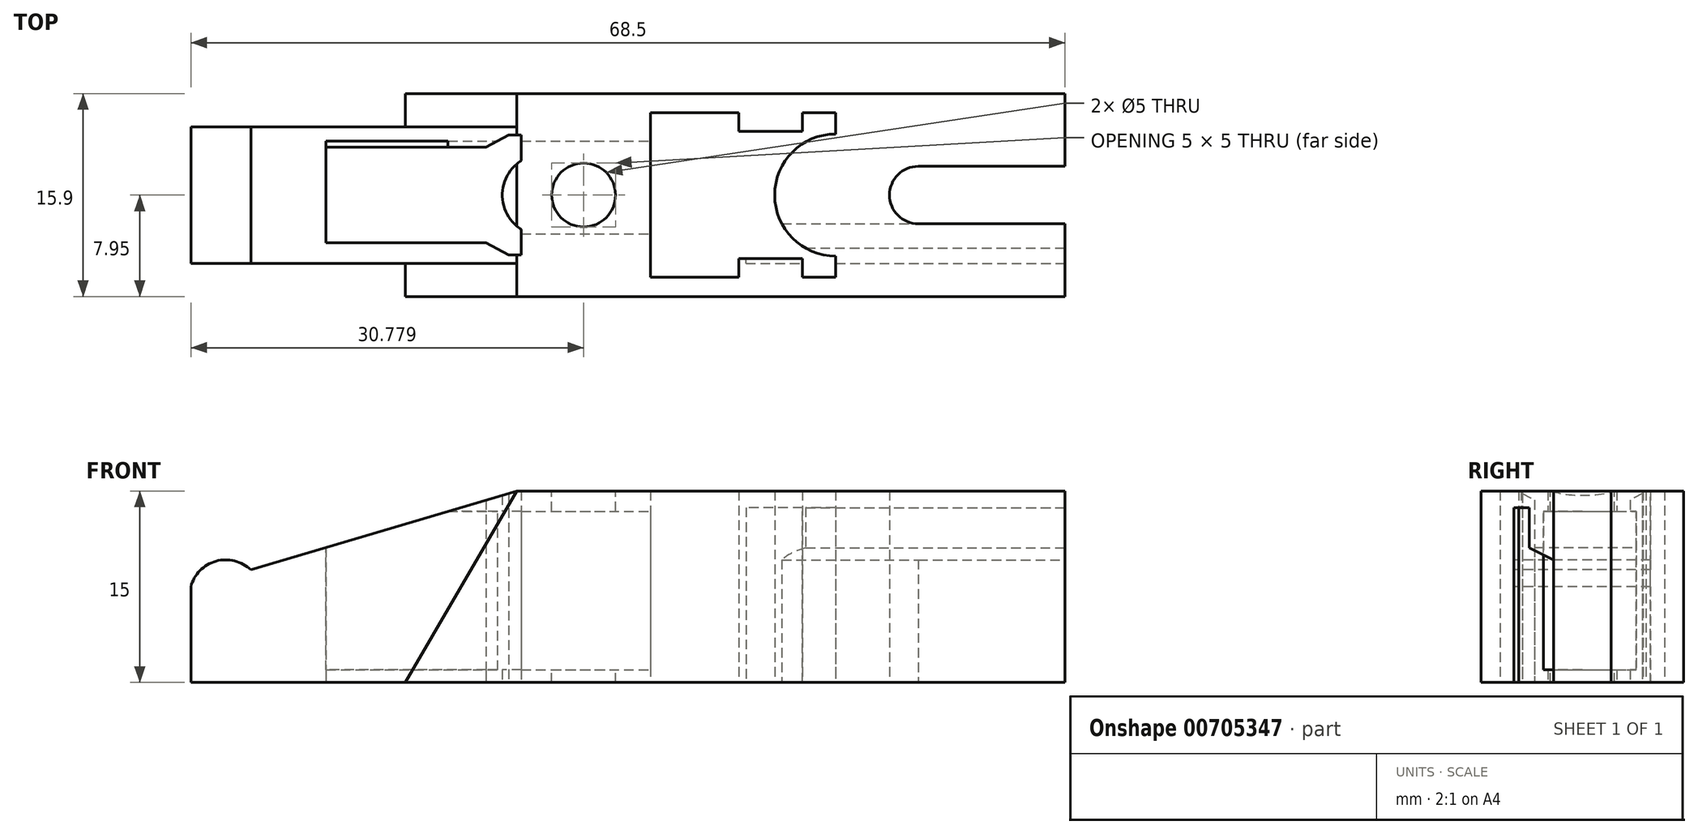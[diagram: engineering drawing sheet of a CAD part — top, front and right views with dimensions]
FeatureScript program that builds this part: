
annotation { "Feature Type Name" : "Feature", "Feature Type Description" : "" }
export const myFeature = defineFeature(function(context is Context, id is Id, definition is map)
    precondition{}
    {
        {
            var Q0;
            Q0=qCreatedBy(makeId("Top.planeOp"),FACE);
            var sketch = newSketch(context, id + "F0", { "sketchPlane" : qUnion([Q0])});
            skLineSegment(sketch, "E0", {"start": v(0, 0) * mm, "end": v(0, 10.7) * mm});
            skLineSegment(sketch, "E1", {"start": v(0, 10.7) * mm, "end": v(16.8, 10.7) * mm});
            skLineSegment(sketch, "E2", {"start": v(68.5, 13.3) * mm, "end": v(68.5, 7.6) * mm});
            skLineSegment(sketch, "E3", {"start": v(68.5, 7.6) * mm, "end": v(57, 7.6) * mm});
            skLineSegment(sketch, "E4", {"start": v(57, 3.1) * mm, "end": v(68.5, 3.1) * mm});
            skLineSegment(sketch, "E5", {"start": v(0, 0) * mm, "end": v(16.8, 0) * mm});
            skLineSegment(sketch, "E6", {"start": v(16.8, 0) * mm, "end": v(16.8, -2.6) * mm});
            skLineSegment(sketch, "E7", {"start": v(16.8, -2.6) * mm, "end": v(68.5, -2.6) * mm});
            skLineSegment(sketch, "E8", {"start": v(68.5, -2.6) * mm, "end": v(68.5, 3.1) * mm});
            skLineSegment(sketch, "E9", {"start": v(50.53, -1.1) * mm, "end": v(50.53, 0.57) * mm});
            skLineSegment(sketch, "E10", {"start": v(25.9, 0.66) * mm, "end": v(25.9, 2.66) * mm});
            skLineSegment(sketch, "E11.MirrorCS", {"start": v(10.6, 9.1) * mm, "end": v(23.13, 9.1) * mm});
            skLineSegment(sketch, "E12.MirrorCS", {"start": v(25.9, 10.04) * mm, "end": v(25.9, 8.04) * mm});
            skArc(sketch, "E13", {"start": v(25.9, 8.04) * mm, "mid": v(24.4, 5.35) * mm, "end": v(25.9, 2.66) * mm});
            skLineSegment(sketch, "E14.MirrorCS", {"start": v(16.8, 10.7) * mm, "end": v(16.8, 13.3) * mm});
            skLineSegment(sketch, "E15.MirrorCS", {"start": v(16.8, 13.3) * mm, "end": v(68.5, 13.3) * mm});
            skLineSegment(sketch, "E16", {"start": v(36.03, -1.1) * mm, "end": v(42.93, -1.1) * mm});
            skLineSegment(sketch, "E17", {"start": v(42.93, -1.1) * mm, "end": v(42.93, 0.37) * mm});
            skLineSegment(sketch, "E18", {"start": v(42.93, 0.37) * mm, "end": v(47.93, 0.37) * mm});
            skLineSegment(sketch, "E19", {"start": v(47.93, 0.37) * mm, "end": v(47.93, -1.1) * mm});
            skLineSegment(sketch, "E20", {"start": v(47.93, -1.1) * mm, "end": v(50.53, -1.1) * mm});
            skLineSegment(sketch, "E21.MirrorCS", {"start": v(23.13, 9.1) * mm, "end": v(24.9, 10.04) * mm});
            skLineSegment(sketch, "E22.MirrorCS", {"start": v(24.9, 10.04) * mm, "end": v(25.9, 10.04) * mm});
            skPoint(sketch, "E23", {"position": v(24.4, 5.35) * mm});
            skLineSegment(sketch, "E24", {"start": v(57, 7.6) * mm, "end": v(57, 3.1) * mm, "construction": true});
            skArc(sketch, "E25", {"start": v(57, 7.6) * mm, "mid": v(54.75, 5.35) * mm, "end": v(57, 3.1) * mm});
            skLineSegment(sketch, "E26", {"start": v(0, 5.35) * mm, "end": v(68.5, 5.35) * mm, "construction": true});
            skLineSegment(sketch, "E27.MirrorCS", {"start": v(10.6, 1.6) * mm, "end": v(23.13, 1.6) * mm});
            skLineSegment(sketch, "E28.MirrorCS", {"start": v(23.13, 1.6) * mm, "end": v(24.9, 0.66) * mm});
            skLineSegment(sketch, "E29.MirrorCS", {"start": v(24.9, 0.66) * mm, "end": v(25.9, 0.66) * mm});
            skLineSegment(sketch, "E30", {"start": v(10.6, 9.1) * mm, "end": v(10.6, 1.6) * mm});
            skLineSegment(sketch, "E31", {"start": v(36.03, 11.8) * mm, "end": v(36.03, -1.1) * mm});
            skLineSegment(sketch, "E32.MirrorCS", {"start": v(36.03, 11.8) * mm, "end": v(42.93, 11.8) * mm});
            skLineSegment(sketch, "E33.MirrorCS", {"start": v(42.93, 11.8) * mm, "end": v(42.93, 10.33) * mm});
            skLineSegment(sketch, "E34.MirrorCS", {"start": v(42.93, 10.33) * mm, "end": v(47.93, 10.33) * mm});
            skLineSegment(sketch, "E35.MirrorCS", {"start": v(47.93, 10.33) * mm, "end": v(47.93, 11.8) * mm});
            skLineSegment(sketch, "E36.MirrorCS", {"start": v(47.93, 11.8) * mm, "end": v(50.53, 11.8) * mm});
            skLineSegment(sketch, "E37.MirrorCS", {"start": v(50.53, 11.8) * mm, "end": v(50.53, 10.13) * mm});
            skLineSegment(sketch, "E38", {"start": v(50.53, 10.13) * mm, "end": v(50.53, 0.57) * mm, "construction": true});
            skArc(sketch, "E39", {"start": v(50.53, 10.13) * mm, "mid": v(45.75, 5.35) * mm, "end": v(50.53, 0.57) * mm});
            skPoint(sketch, "E40", {"position": v(45.75, 5.35) * mm});
            skSolve(sketch);
        }
        {
            var Q0;
            Q0 = qSketchRegion(id + "F0", true);
            var Q1;
            Q1=makeQuery(id+"F0.imprint","IMPRINT",FACE,{"disambiguationData":[TD([[makeQuery(id+"F0.imprint","IMPRINT",EDGE,{"derivedFrom":sQuery(id+"F0.wireOp",EDGE,"E0")}),-1.0]])]});
            extrude(context, id + "F1", {"entities" : qUnion([Q0, Q1]), "depth" : 15 * mm, "offsetDistance" : 25 * mm});
        }
        {
            var Q0;
            Q0=makeQuery(id+"F1.opExtrude","SWEPT_FACE",FACE,{"disambiguationData":[OSD([sQuery(id+"F0.wireOp",EDGE,"E7")])]});
            var sketch = newSketch(context, id + "F2", { "sketchPlane" : qUnion([Q0])});
            skLineSegment(sketch, "E41", {"start": v(16.8, 0) * mm, "end": v(25.53, 15) * mm});
            skLineSegment(sketch, "E42", {"start": v(25.53, 15) * mm, "end": v(16.8, 15) * mm});
            skLineSegment(sketch, "E43", {"start": v(16.8, 15) * mm, "end": v(16.8, 0) * mm});
            skSolve(sketch);
        }
        {
            var Q0;
            Q0 = qSketchRegion(id + "F2", true);
            var Q1;
            Q1=makeQuery(id+"F1.opExtrude","SWEPT_FACE",FACE,{"disambiguationData":[OSD([sQuery(id+"F0.wireOp",EDGE,"E5")])]});
            extrude(context, id + "F3", {"entities" : qUnion([Q0]), "operationType" : NewBodyOperationType.REMOVE, "endBound" : BoundingType.UP_TO_SURFACE, "oppositeDirection" : true, "depth" : 25 * mm, "endBoundEntityFace" : qUnion([Q1]), "offsetDistance" : 25 * mm});
        }
        {
            var Q0;
            Q0=makeQuery(id+"F1.opExtrude","SWEPT_FACE",FACE,{"disambiguationData":[OSD([sQuery(id+"F0.wireOp",EDGE,"E15.MirrorCS")])]});
            var sketch = newSketch(context, id + "F4", { "sketchPlane" : qUnion([Q0])});
            skLineSegment(sketch, "E44", {"start": v(-16.8, 0) * mm, "end": v(-16.8, 15) * mm});
            skLineSegment(sketch, "E45", {"start": v(-16.8, 15) * mm, "end": v(-25.53, 15) * mm});
            skLineSegment(sketch, "E46", {"start": v(-25.53, 15) * mm, "end": v(-16.8, 0) * mm});
            skSolve(sketch);
        }
        {
            var Q0;
            Q0 = qSketchRegion(id + "F4", true);
            var Q1;
            Q1=makeQuery(id+"F1.opExtrude","SWEPT_FACE",FACE,{"disambiguationData":[OSD([sQuery(id+"F0.wireOp",EDGE,"E1")])]});
            extrude(context, id + "F5", {"entities" : qUnion([Q0]), "operationType" : NewBodyOperationType.REMOVE, "endBound" : BoundingType.UP_TO_SURFACE, "oppositeDirection" : true, "depth" : 25 * mm, "endBoundEntityFace" : qUnion([Q1]), "offsetDistance" : 25 * mm});
        }
        {
            var Q0;
            Q0=makeQuery(id+"F1.opExtrude","CAP_FACE",FACE,{"disambiguationData":[OSD([sQuery(id+"F0.wireOp",EDGE,"E0"),sQuery(id+"F0.wireOp",EDGE,"E1"),sQuery(id+"F0.wireOp",EDGE,"E2"),sQuery(id+"F0.wireOp",EDGE,"E3"),sQuery(id+"F0.wireOp",EDGE,"E4"),sQuery(id+"F0.wireOp",EDGE,"E5"),sQuery(id+"F0.wireOp",EDGE,"E6"),sQuery(id+"F0.wireOp",EDGE,"E7"),sQuery(id+"F0.wireOp",EDGE,"E8"),sQuery(id+"F0.wireOp",EDGE,"E9"),sQuery(id+"F0.wireOp",EDGE,"E10"),sQuery(id+"F0.wireOp",EDGE,"E11.MirrorCS"),sQuery(id+"F0.wireOp",EDGE,"E12.MirrorCS"),sQuery(id+"F0.wireOp",EDGE,"E13"),sQuery(id+"F0.wireOp",EDGE,"E14.MirrorCS"),sQuery(id+"F0.wireOp",EDGE,"E15.MirrorCS"),sQuery(id+"F0.wireOp",EDGE,"E16"),sQuery(id+"F0.wireOp",EDGE,"E17"),sQuery(id+"F0.wireOp",EDGE,"E18"),sQuery(id+"F0.wireOp",EDGE,"E19"),sQuery(id+"F0.wireOp",EDGE,"E20"),sQuery(id+"F0.wireOp",EDGE,"E21.MirrorCS"),sQuery(id+"F0.wireOp",EDGE,"E22.MirrorCS"),sQuery(id+"F0.wireOp",EDGE,"E25"),sQuery(id+"F0.wireOp",EDGE,"E27.MirrorCS"),sQuery(id+"F0.wireOp",EDGE,"E28.MirrorCS"),sQuery(id+"F0.wireOp",EDGE,"E29.MirrorCS"),sQuery(id+"F0.wireOp",EDGE,"E30"),sQuery(id+"F0.wireOp",EDGE,"E31"),sQuery(id+"F0.wireOp",EDGE,"E32.MirrorCS"),sQuery(id+"F0.wireOp",EDGE,"E33.MirrorCS"),sQuery(id+"F0.wireOp",EDGE,"E34.MirrorCS"),sQuery(id+"F0.wireOp",EDGE,"E35.MirrorCS"),sQuery(id+"F0.wireOp",EDGE,"E36.MirrorCS"),sQuery(id+"F0.wireOp",EDGE,"E37.MirrorCS"),sQuery(id+"F0.wireOp",EDGE,"E39")])],"isStart":false});
            var sketch = newSketch(context, id + "F6", { "sketchPlane" : qUnion([Q0])});
            skCircle(sketch, "E47", {"center": v(30.78, 5.35) * mm, "radius": 2.5 * mm});
            skPoint(sketch, "E47.centerSnap0", {"position": v(36.03, 5.35) * mm});
            skSolve(sketch);
        }
        {
            var Q0;
            Q0 = qSketchRegion(id + "F6", true);
            extrude(context, id + "F7", {"entities" : qUnion([Q0]), "operationType" : NewBodyOperationType.REMOVE, "endBound" : BoundingType.THROUGH_ALL, "oppositeDirection" : true, "depth" : 25 * mm, "offsetDistance" : 25 * mm});
        }
        {
            var Q0;
            Q0=makeQuery(id+"F1.opExtrude","SWEPT_FACE",FACE,{"disambiguationData":[OSD([sQuery(id+"F0.wireOp",EDGE,"E8")])]});
            var sketch = newSketch(context, id + "F8", { "sketchPlane" : qUnion([Q0])});
            skLineSegment(sketch, "E48", {"start": v(0, 0) * mm, "end": v(0, 13.7) * mm});
            skLineSegment(sketch, "E49", {"start": v(0, 13.7) * mm, "end": v(1.18, 13.7) * mm});
            skLineSegment(sketch, "E50", {"start": v(1.18, 13.7) * mm, "end": v(1.18, 10.55) * mm});
            skLineSegment(sketch, "E51", {"start": v(1.18, 10.55) * mm, "end": v(3.1, 9.61) * mm});
            skLineSegment(sketch, "E52", {"start": v(3.1, 9.61) * mm, "end": v(3.1, 11.46) * mm});
            skLineSegment(sketch, "E53", {"start": v(3.1, 11.46) * mm, "end": v(2.48, 11.7) * mm});
            skLineSegment(sketch, "E54", {"start": v(2.48, 11.7) * mm, "end": v(2.48, 15) * mm});
            skLineSegment(sketch, "E55", {"start": v(2.48, 15) * mm, "end": v(-2.6, 15) * mm});
            skLineSegment(sketch, "E56", {"start": v(-2.6, 15) * mm, "end": v(-2.6, 0) * mm});
            skLineSegment(sketch, "E57", {"start": v(5.37, 15.07) * mm, "end": v(5.37, -0.31) * mm, "construction": true});
            skLineSegment(sketch, "E58.MirrorCS", {"start": v(8.27, 11.7) * mm, "end": v(8.27, 15) * mm});
            skLineSegment(sketch, "E59.MirrorCS", {"start": v(7.65, 11.46) * mm, "end": v(8.27, 11.7) * mm});
            skLineSegment(sketch, "E60.MirrorCS", {"start": v(9.57, 10.55) * mm, "end": v(7.65, 9.61) * mm});
            skLineSegment(sketch, "E61.MirrorCS", {"start": v(9.57, 13.7) * mm, "end": v(9.57, 10.55) * mm});
            skLineSegment(sketch, "E62.MirrorCS", {"start": v(10.75, 13.7) * mm, "end": v(9.57, 13.7) * mm});
            skLineSegment(sketch, "E63.MirrorCS", {"start": v(10.75, 0) * mm, "end": v(10.75, 13.7) * mm});
            skLineSegment(sketch, "E64.MirrorCS", {"start": v(13.35, 15) * mm, "end": v(13.35, 0) * mm});
            skLineSegment(sketch, "E65.MirrorCS", {"start": v(8.27, 15) * mm, "end": v(13.35, 15) * mm});
            skLineSegment(sketch, "E66", {"start": v(-2.6, 0) * mm, "end": v(0, 0) * mm});
            skSolve(sketch);
        }
        {
            var Q0;
            {var subQ5=sQuery(id+"F8.wireOp",EDGE,"E48");Q0=makeQuery(id+"F8.imprint","IMPRINT",FACE,{"disambiguationData":[TD([[makeQuery(id+"F8.imprint","IMPRINT",EDGE,{"derivedFrom":subQ5}),-1.0]])]});}
            extrude(context, id + "F9", {"entities" : qUnion([Q0]), "operationType" : NewBodyOperationType.REMOVE, "oppositeDirection" : true, "depth" : 25 * mm, "offsetDistance" : 25 * mm});
        }
        {
            var Q0;
            Q0=makeQuery(id+"F1.opExtrude","SWEPT_FACE",FACE,{"disambiguationData":[OSD([sQuery(id+"F0.wireOp",EDGE,"E31")])]});
            var sketch = newSketch(context, id + "F10", { "sketchPlane" : qUnion([Q0])});
            skLineSegment(sketch, "E67.bottom", {"start": v(2.32, 13.4) * mm, "end": v(9.58, 13.4) * mm});
            skLineSegment(sketch, "E67.top", {"start": v(2.32, 0.98) * mm, "end": v(9.58, 0.98) * mm});
            skLineSegment(sketch, "E67.left", {"start": v(2.32, 13.4) * mm, "end": v(2.32, 0.98) * mm});
            skLineSegment(sketch, "E67.right", {"start": v(9.58, 13.4) * mm, "end": v(9.58, 0.98) * mm});
            skSolve(sketch);
        }
        {
            var Q0;
            Q0 = qSketchRegion(id + "F10", true);
            var Q1;
            Q1=makeQuery(id+"F1.opExtrude","SWEPT_FACE",FACE,{"disambiguationData":[OSD([sQuery(id+"F0.wireOp",EDGE,"E30")])]});
            extrude(context, id + "F11", {"entities" : qUnion([Q0]), "operationType" : NewBodyOperationType.REMOVE, "endBound" : BoundingType.UP_TO_SURFACE, "oppositeDirection" : true, "depth" : 25 * mm, "endBoundEntityFace" : qUnion([Q1]), "offsetDistance" : 25 * mm});
        }
        {
            var Q0;
            {var subQ0=sQuery(id+"F0.wireOp",EDGE,"E5");Q0=makeQuery(id+"F3.boolean.opBoolean","MERGE",FACE,{"derivedFrom":[makeQuery(id+"F1.opExtrude","SWEPT_FACE",FACE,{"disambiguationData":[OSD([subQ0])]}),makeQuery(id+"F3.opExtrude","CAP_FACE",FACE,{"disambiguationData":[OSD([subQ0])],"isStart":false})]});}
            var sketch = newSketch(context, id + "F12", { "sketchPlane" : qUnion([Q0])});
            skArc(sketch, "E68", {"start": v(4.7, 8.82) * mm, "mid": v(1.97, 9.5) * mm, "end": v(0, 7.5) * mm});
            skLineSegment(sketch, "E69", {"start": v(4.7, 8.82) * mm, "end": v(25.53, 15) * mm});
            skLineSegment(sketch, "E70", {"start": v(25.53, 15) * mm, "end": v(16.8, 0) * mm});
            skLineSegment(sketch, "E71", {"start": v(16.8, 0) * mm, "end": v(0, 0) * mm});
            skLineSegment(sketch, "E72", {"start": v(0, 0) * mm, "end": v(0, 7.5) * mm});
            skSolve(sketch);
        }
        {
            var Q0;
            {var subQ0=sQuery(id+"F12.wireOp",EDGE,"E68");Q0=makeQuery(id+"F12.imprint","IMPRINT",FACE,{"disambiguationData":[TD([[makeQuery(id+"F12.imprint","IMPRINT",EDGE,{"derivedFrom":subQ0}),-1.0]])]});}
            extrude(context, id + "F13", {"entities" : qUnion([Q0]), "operationType" : NewBodyOperationType.REMOVE, "endBound" : BoundingType.THROUGH_ALL, "oppositeDirection" : true, "depth" : 25 * mm, "offsetDistance" : 25 * mm});
        }
    });
